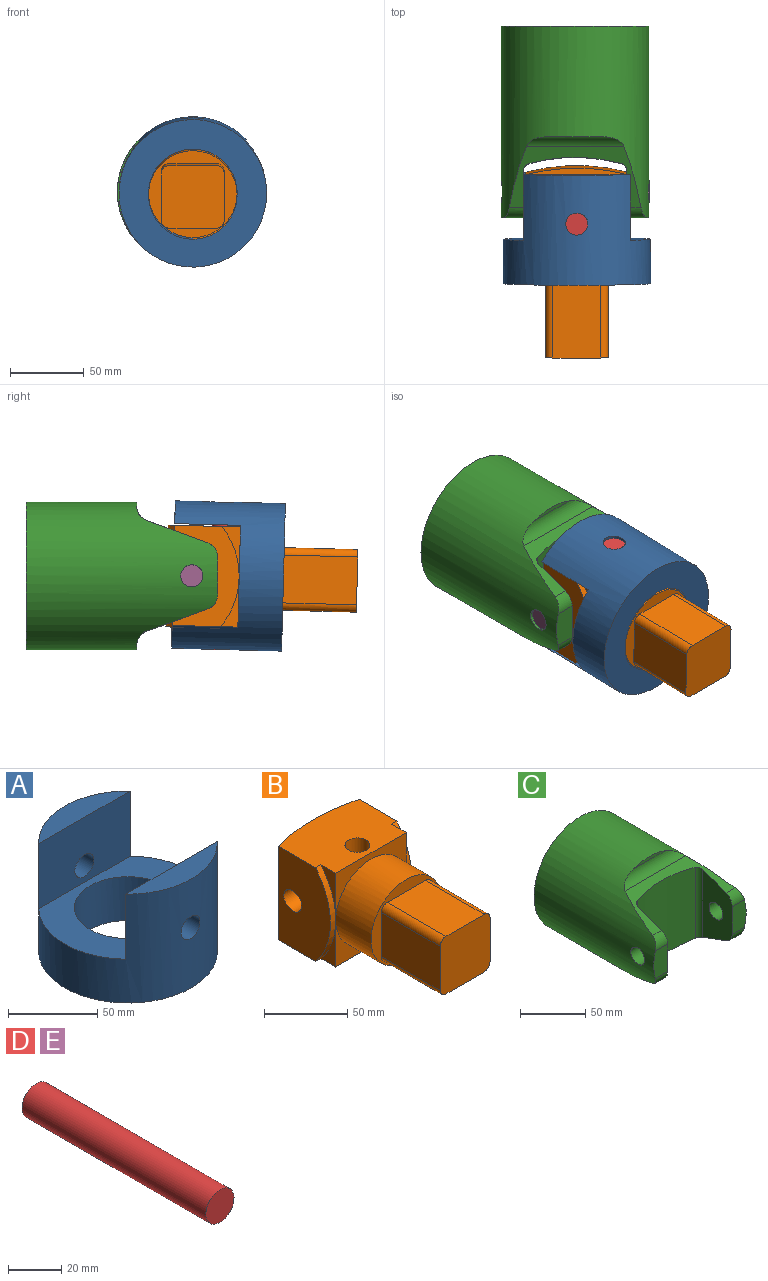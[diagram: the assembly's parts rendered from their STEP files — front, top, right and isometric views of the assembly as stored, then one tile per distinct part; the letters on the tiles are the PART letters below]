
ASSEMBLY  parts=5 mates=4
PART A: 10 faces, bbox 100x100x74.6 mm
  f0: plane 72.38x15.5mm, normal (0,0,1), area 774.7mm2, adj f1,f6
  f1: cylinder r=50mm len=100mm, axis (0,0,-1), area 16285.6mm2, adj f0,f2,f3,f4,f5,f6,f7,f8
  f2: plane 72.38x15.5mm, normal (0,0,1), area 774.7mm2, adj f1,f5
  f3: plane 100x100mm, normal (0,0,-1), area 5026.5mm2, adj f1,f9
  f4: plane 100x69mm, normal (0,0,1), area 3477.2mm2, adj f1,f5,f6,f9
  f5: plane 72.38x44.59mm, normal (0,-1,0), area 3050.4mm2, adj f1,f2,f4,f8
  f6: plane 72.38x44.59mm, normal (0,1,0), area 3050.4mm2, adj f0,f1,f4,f7
  f7: cylinder r=7.5mm len=15.5mm, axis (0,-1,0), area 717.1mm2, adj f1,f6
  f8: cylinder r=7.5mm len=15.5mm, axis (0,-1,0), area 717.1mm2, adj f1,f5
  f9: cylinder r=30mm len=60mm, axis (0,0,-1), area 5654.9mm2, adj f3,f4
PART B: 26 faces, bbox 69x129.1x69 mm
  f0: plane 69x49.08mm, normal (0,0,1), area 2993.4mm2, adj f1,f3,f5,f17,f18,f20,f21,f23
  f1: plane 69x44.59mm, normal (1,0,0), area 2624.3mm2, adj f0,f2,f17,f21,f24
  f2: plane 69x49.08mm, normal (0,0,-1), area 2993.4mm2, adj f1,f4,f5,f17,f18,f19,f21,f22
  f3: plane 60x34.5mm, normal (0,-1,0), area 656.3mm2, adj f0,f6,f20,f23
  f4: plane 60x34.5mm, normal (0,-1,0), area 656.3mm2, adj f2,f6,f19,f22
  f5: plane 69x44.59mm, normal (-1,0,0), area 2624.3mm2, adj f0,f2,f17,f18,f24
  f6: cylinder r=30mm len=60mm, axis (0,-1,0), area 5654.9mm2, adj f3,f4,f15
  f7: cylinder r=5mm len=50mm, axis (0,-1,0), area 392.7mm2, adj f8,f14,f15,f16
  f8: plane 50x32.43mm, normal (1,0,0), area 1621.3mm2, adj f7,f9,f15,f16
  f9: cylinder r=5mm len=50mm, axis (0,-1,0), area 392.7mm2, adj f8,f10,f15,f16
  f10: plane 50x32.43mm, normal (0,0,-1), area 1621.3mm2, adj f9,f11,f15,f16
  f11: cylinder r=5mm len=50mm, axis (0,-1,0), area 392.7mm2, adj f10,f12,f15,f16
  f12: plane 50x32.43mm, normal (-1,0,0), area 1621.3mm2, adj f11,f13,f15,f16
  f13: cylinder r=5mm len=50mm, axis (0,-1,0), area 392.7mm2, adj f12,f14,f15,f16
  f14: plane 50x32.43mm, normal (0,0,1), area 1621.3mm2, adj f7,f13,f15,f16
  f15: plane 60x60mm, normal (0,-1,0), area 1048.9mm2, adj f6,f7,f8,f9,f10,f11,f12,f13
  f16: plane 42.43x42.43mm, normal (0,-1,0), area 1778.5mm2, adj f7,f8,f9,f10,f11,f12,f13,f14
  f17: cylinder r=134.66mm len=69mm, axis (0,0,1), area 4814.7mm2, adj f0,f1,f2,f5
  f18: cylinder r=53.4mm len=69mm, axis (-1,0,0), area 337.6mm2, adj f0,f2,f5,f19,f20
  f19: plane 34.5x12.64mm, normal (-1,0,0), area 137.7mm2, adj f2,f4,f18
  f20: plane 34.5x12.64mm, normal (-1,0,0), area 137.7mm2, adj f0,f3,f18
  f21: cylinder r=53.4mm len=69mm, axis (1,0,0), area 337.6mm2, adj f0,f1,f2,f22,f23
  f22: plane 34.5x12.64mm, normal (1,0,0), area 137.7mm2, adj f2,f4,f21
  f23: plane 34.5x12.64mm, normal (1,0,0), area 137.7mm2, adj f0,f3,f21
  f24: cylinder r=7.5mm len=69mm, axis (-1,0,0), area 3251.5mm2, adj f1,f5
  f25: cylinder r=7.5mm len=69mm, axis (0,0,1), area 3251.5mm2, adj f0,f2
PART C: 21 faces, bbox 100x129.9x100 mm
  f0: cylinder r=50mm len=129.85mm, axis (0,1,0), area 30382.3mm2, adj f1,f2,f3,f4,f5,f6,f7,f8
  f1: cylinder r=10mm len=13.28mm, axis (1,0,0), area 139.2mm2, adj f0,f2,f7,f18
  f2: plane 26x15mm, normal (0,-1,0), area 375.3mm2, adj f0,f1,f3,f18
  f3: cylinder r=10mm len=13.28mm, axis (1,0,0), area 139.2mm2, adj f0,f2,f11,f18
  f4: plane 100x100mm, normal (0,1,0), area 7854mm2, adj f0
  f5: plane 34.13x3mm, normal (0,-1,0), area 68.7mm2, adj f0,f6
  f6: cylinder r=10mm len=65.91mm, axis (1,0,0), area 664.4mm2, adj f0,f5,f7
  f7: plane 89.41x41.7mm, normal (0,-0.34,-0.94), area 1097.5mm2, adj f0,f1,f6,f8,f14,f15,f16,f17
  f8: cylinder r=10mm len=13.28mm, axis (1,0,0), area 139.2mm2, adj f0,f7,f9,f14
  f9: plane 26x15mm, normal (0,-1,0), area 375.3mm2, adj f0,f8,f10,f14
  f10: cylinder r=10mm len=13.28mm, axis (1,0,0), area 139.2mm2, adj f0,f9,f11,f14
  f11: plane 89.41x41.7mm, normal (0,-0.34,0.94), area 1097.5mm2, adj f0,f3,f10,f12,f14,f15,f16,f17
  f12: cylinder r=10mm len=65.91mm, axis (1,0,0), area 664.4mm2, adj f0,f11,f13
  f13: plane 34.13x3mm, normal (0,-1,0), area 68.7mm2, adj f0,f12
  f14: plane 63.18x31.79mm, normal (-1,0,0), area 1445.6mm2, adj f7,f8,f9,f10,f11,f15,f20
  f15: cylinder r=5mm len=66.7mm, axis (0,0,1), area 423.7mm2, adj f7,f11,f14,f16
  f16: cylinder r=116.73mm len=69.83mm, axis (0,0,1), area 4364.9mm2, adj f7,f11,f15,f17
  f17: cylinder r=5mm len=66.7mm, axis (0,0,1), area 423.7mm2, adj f7,f11,f16,f18
  f18: plane 63.18x31.79mm, normal (1,0,0), area 1445.6mm2, adj f1,f2,f3,f7,f11,f17,f19
  f19: cylinder r=7.5mm len=15mm, axis (-1,0,0), area 693.6mm2, adj f0,f18
  f20: cylinder r=7.5mm len=15mm, axis (-1,0,0), area 693.5mm2, adj f0,f14
PART D: 3 faces, bbox 15x98x15 mm
  f0: cylinder r=7.5mm len=98mm, axis (0,1,0), area 4618.1mm2, adj f1,f2
  f1: plane 15x15mm, normal (0,-1,0), area 176.7mm2, adj f0
  f2: plane 15x15mm, normal (0,1,0), area 176.7mm2, adj f0
PART E: same geometry as D
PLACE A rot(axis=(-1,0,0),88.5deg) t=(-188.11,-637.13,-508)mm
PLACE B rot(axis=(1,0,0),1.5deg) t=(-188.14,-557.14,-506.54)mm
PLACE C t=(-189.24,-462.7,-507)mm fixed
PLACE D rot(axis=(-0.57,0.59,-0.57),119.1deg) t=(-188.14,-594.35,-557.02)mm
PLACE E rot(axis=(0,0,-1),90deg) t=(-139.14,-575.05,-507)mm
MATE revolute D.f0 <-> B.f25  axis (0,0.03,-1) through (-188.14,-595.62,-508.03)mm
MATE fastened A.f7 <-> D.f0  axis (0,-0.03,1) through (-188.14,-594.35,-557.02)mm
MATE fastened E.f0 <-> C.f19  axis (1,0,0) through (-139.14,-575.05,-507)mm
MATE revolute E.f0 <-> B.f24  axis (1,0,0) through (-188.14,-575.05,-507)mm
